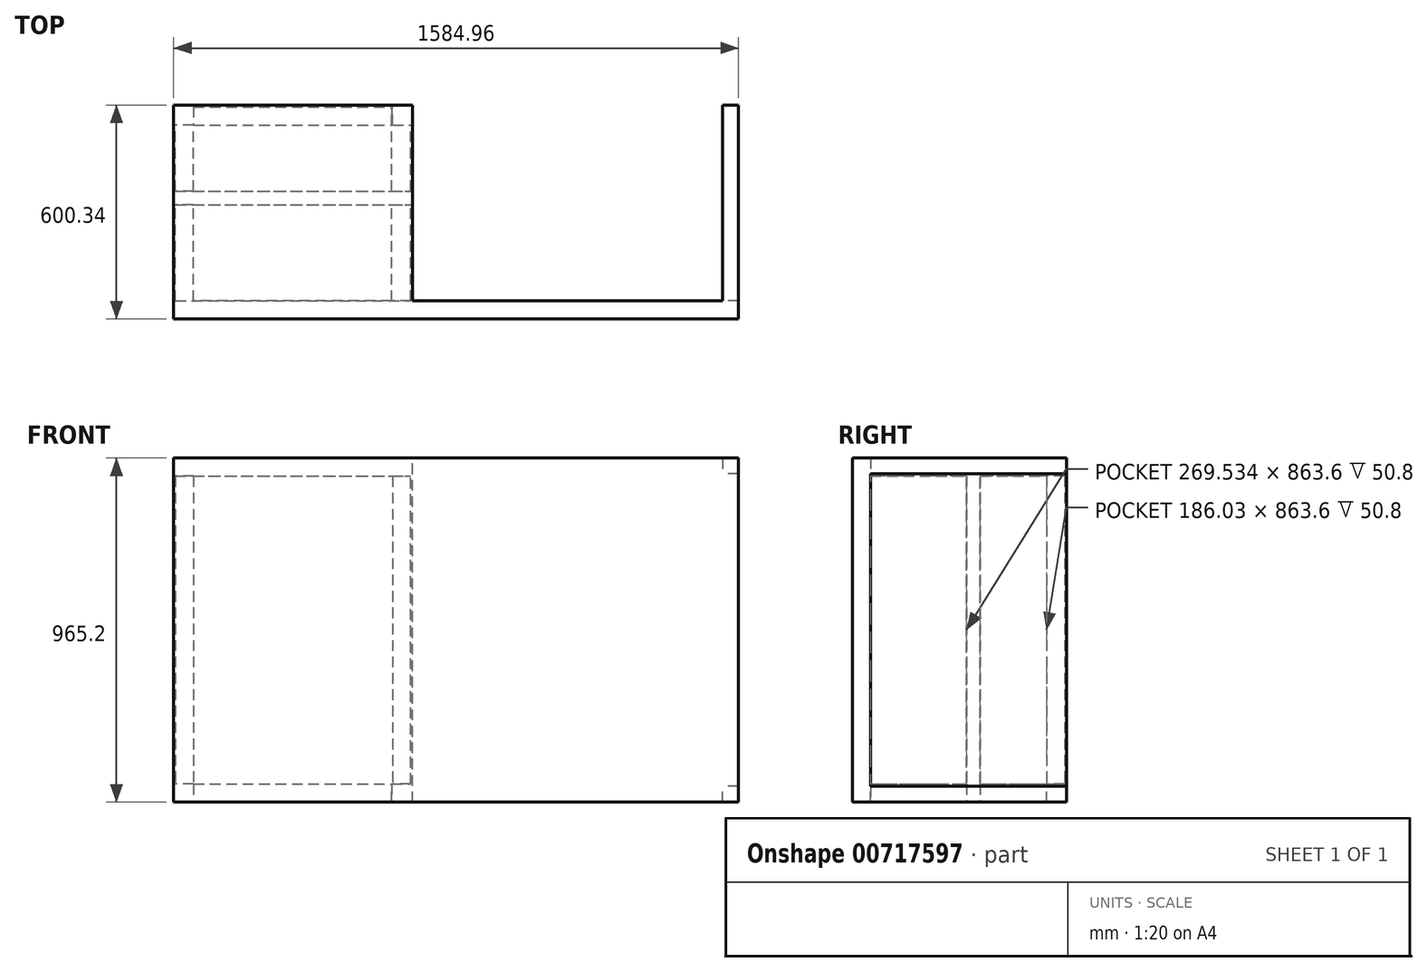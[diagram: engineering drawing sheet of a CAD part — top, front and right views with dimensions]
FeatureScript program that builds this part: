
annotation { "Feature Type Name" : "Feature", "Feature Type Description" : "" }
export const myFeature = defineFeature(function(context is Context, id is Id, definition is map)
    precondition{}
    {
        {
            var Q0;
            Q0=qCreatedBy(makeId("Top.planeOp"),FACE);
            var sketch = newSketch(context, id + "F0", { "sketchPlane" : qUnion([Q0])});
            skLineSegment(sketch, "E0.bottom", {"start": v(-609.6, -762) * mm, "end": v(609.6, -762) * mm});
            skLineSegment(sketch, "E0.top", {"start": v(-609.6, 762) * mm, "end": v(609.6, 762) * mm});
            skLineSegment(sketch, "E0.left", {"start": v(-609.6, -762) * mm, "end": v(-609.6, 762) * mm});
            skLineSegment(sketch, "E0.right", {"start": v(609.6, -762) * mm, "end": v(609.6, 762) * mm});
            skPoint(sketch, "E0.middle", {"position": v(0, 0) * mm});
            skLineSegment(sketch, "E1.0", {"start": v(660.4, -812.8) * mm, "end": v(660.4, 812.8) * mm});
            skLineSegment(sketch, "E1.1", {"start": v(-660.4, -812.8) * mm, "end": v(660.4, -812.8) * mm});
            skLineSegment(sketch, "E1.2", {"start": v(-660.4, -812.8) * mm, "end": v(-660.4, 812.8) * mm});
            skLineSegment(sketch, "E1.3", {"start": v(-660.4, 812.8) * mm, "end": v(660.4, 812.8) * mm});
            skSolve(sketch);
        }
        {
            var Q0;
            Q0=makeQuery(id+"F0.imprint","IMPRINT",FACE,{"disambiguationData":[TD([[makeQuery(id+"F0.imprint","IMPRINT",EDGE,{"derivedFrom":sQuery(id+"F0.wireOp",EDGE,"E0.bottom")}),-1.0]])]});
            extrude(context, id + "F1", {"entities" : qUnion([Q0]), "depth" : 50.8 * mm, "offsetDistance" : 25.4 * mm});
        }
        {
            var Q0;
            Q0=makeQuery(id+"F1.opExtrude","CAP_FACE",FACE,{"disambiguationData":[OSD([sQuery(id+"F0.wireOp",EDGE,"E0.bottom"),sQuery(id+"F0.wireOp",EDGE,"E0.top"),sQuery(id+"F0.wireOp",EDGE,"E0.left"),sQuery(id+"F0.wireOp",EDGE,"E0.right"),sQuery(id+"F0.wireOp",EDGE,"E1.0"),sQuery(id+"F0.wireOp",EDGE,"E1.1"),sQuery(id+"F0.wireOp",EDGE,"E1.2"),sQuery(id+"F0.wireOp",EDGE,"E1.3")])],"isStart":false});
            var sketch = newSketch(context, id + "F2", { "sketchPlane" : qUnion([Q0])});
            skLineSegment(sketch, "E2", {"start": v(-660.4, 812.8) * mm, "end": v(-609.6, 812.8) * mm});
            skLineSegment(sketch, "E3", {"start": v(-609.6, 812.8) * mm, "end": v(-609.6, 762) * mm});
            skLineSegment(sketch, "E4", {"start": v(-609.6, 762) * mm, "end": v(-660.4, 762) * mm});
            skLineSegment(sketch, "E5", {"start": v(-660.4, 762) * mm, "end": v(-660.4, 812.8) * mm});
            skLineSegment(sketch, "E6.MirrorCS", {"start": v(660.4, 812.8) * mm, "end": v(609.6, 812.8) * mm});
            skLineSegment(sketch, "E7.MirrorCS", {"start": v(609.6, 812.8) * mm, "end": v(609.6, 762) * mm});
            skLineSegment(sketch, "E8.MirrorCS", {"start": v(660.4, 762) * mm, "end": v(660.4, 812.8) * mm});
            skLineSegment(sketch, "E9.MirrorCS", {"start": v(609.6, 762) * mm, "end": v(660.4, 762) * mm});
            skLineSegment(sketch, "E10.MirrorCS", {"start": v(609.6, -762) * mm, "end": v(660.4, -762) * mm});
            skLineSegment(sketch, "E11.MirrorCS", {"start": v(-660.4, -812.8) * mm, "end": v(-609.6, -812.8) * mm});
            skLineSegment(sketch, "E12.MirrorCS", {"start": v(-609.6, -812.8) * mm, "end": v(-609.6, -762) * mm});
            skLineSegment(sketch, "E13.MirrorCS", {"start": v(660.4, -762) * mm, "end": v(660.4, -812.8) * mm});
            skLineSegment(sketch, "E14.MirrorCS", {"start": v(-609.6, -762) * mm, "end": v(-660.4, -762) * mm});
            skLineSegment(sketch, "E15.MirrorCS", {"start": v(609.6, -812.8) * mm, "end": v(609.6, -762) * mm});
            skLineSegment(sketch, "E16.MirrorCS", {"start": v(660.4, -812.8) * mm, "end": v(609.6, -812.8) * mm});
            skLineSegment(sketch, "E17.MirrorCS", {"start": v(-660.4, -762) * mm, "end": v(-660.4, -812.8) * mm});
            skSolve(sketch);
        }
        {
            var Q0;
            Q0=qSketchRegion(id+"F2",true);
            extrude(context, id + "F3", {"entities" : qUnion([Q0]), "operationType" : NewBodyOperationType.ADD, "depth" : 863.6 * mm, "offsetDistance" : 25.4 * mm});
        }
        {
            var Q0;
            Q0=makeQuery(id+"F3.opExtrude","CAP_FACE",FACE,{"disambiguationData":[OSD([sQuery(id+"F2.wireOp",EDGE,"E2"),sQuery(id+"F2.wireOp",EDGE,"E3"),sQuery(id+"F2.wireOp",EDGE,"E4"),sQuery(id+"F2.wireOp",EDGE,"E5")])],"isStart":false});
            var sketch = newSketch(context, id + "F4", { "sketchPlane" : qUnion([Q0])});
            skLineSegment(sketch, "E18.bottom", {"start": v(-609.6, -762) * mm, "end": v(609.6, -762) * mm});
            skLineSegment(sketch, "E18.top", {"start": v(-609.6, 762) * mm, "end": v(609.6, 762) * mm});
            skLineSegment(sketch, "E18.left", {"start": v(-609.6, -762) * mm, "end": v(-609.6, 762) * mm});
            skLineSegment(sketch, "E18.right", {"start": v(609.6, -762) * mm, "end": v(609.6, 762) * mm});
            skPoint(sketch, "E18.middle", {"position": v(0, 0) * mm});
            skLineSegment(sketch, "E19.0", {"start": v(-660.4, -812.8) * mm, "end": v(660.4, -812.8) * mm});
            skLineSegment(sketch, "E19.1", {"start": v(-660.4, -812.8) * mm, "end": v(-660.4, 812.8) * mm});
            skLineSegment(sketch, "E19.2", {"start": v(-660.4, 812.8) * mm, "end": v(660.4, 812.8) * mm});
            skLineSegment(sketch, "E19.3", {"start": v(660.4, -812.8) * mm, "end": v(660.4, 812.8) * mm});
            skSolve(sketch);
        }
        {
            var Q0;
            Q0=qSketchRegion(id+"F4",true);
            extrude(context, id + "F5", {"entities" : qUnion([Q0]), "operationType" : NewBodyOperationType.ADD, "depth" : 50.8 * mm, "offsetDistance" : 25.4 * mm});
        }
        {
            var Q0;
            Q0=makeQuery(id+"F5.opExtrude","SWEPT_FACE",FACE,{"disambiguationData":[OSD([sQuery(id+"F4.wireOp",EDGE,"E18.top")])]});
            var sketch = newSketch(context, id + "F6", { "sketchPlane" : qUnion([Q0])});
            skLineSegment(sketch, "E20", {"start": v(-609.6, 914.4) * mm, "end": v(-609.6, 965.2) * mm});
            skLineSegment(sketch, "E21", {"start": v(-609.6, 965.2) * mm, "end": v(0, 965.2) * mm});
            skLineSegment(sketch, "E22", {"start": v(0, 965.2) * mm, "end": v(0, 914.4) * mm});
            skLineSegment(sketch, "E23", {"start": v(0, 914.4) * mm, "end": v(-609.6, 914.4) * mm});
            skSolve(sketch);
        }
        {
            var Q0;
            Q0=qSketchRegion(id+"F6",true);
            extrude(context, id + "F7", {"entities" : qUnion([Q0]), "operationType" : NewBodyOperationType.ADD, "endBound" : BoundingType.UP_TO_NEXT, "depth" : 25.4 * mm, "offsetDistance" : 25.4 * mm});
        }
        {
            var Q0;
            Q0=makeQuery(id+"F7.boolean.opBoolean","MERGE",FACE,{"derivedFrom":[makeQuery(id+"F5.opExtrude","CAP_FACE",FACE,{"disambiguationData":[OSD([sQuery(id+"F4.wireOp",EDGE,"E18.bottom"),sQuery(id+"F4.wireOp",EDGE,"E18.top"),sQuery(id+"F4.wireOp",EDGE,"E18.left"),sQuery(id+"F4.wireOp",EDGE,"E18.right"),sQuery(id+"F4.wireOp",EDGE,"E19.0"),sQuery(id+"F4.wireOp",EDGE,"E19.1"),sQuery(id+"F4.wireOp",EDGE,"E19.2"),sQuery(id+"F4.wireOp",EDGE,"E19.3")])],"isStart":false}),makeQuery(id+"F7.opExtrude","SWEPT_FACE",FACE,{"disambiguationData":[OSD([sQuery(id+"F6.wireOp",EDGE,"E21")])]})]});
            var sketch = newSketch(context, id + "F8", { "sketchPlane" : qUnion([Q0])});
            skLineSegment(sketch, "E24", {"start": v(0, 762) * mm, "end": v(0, 812.8) * mm});
            skLineSegment(sketch, "E25", {"start": v(0, 812.8) * mm, "end": v(660.4, 812.8) * mm});
            skLineSegment(sketch, "E26", {"start": v(660.4, 812.8) * mm, "end": v(660.4, -812.8) * mm});
            skLineSegment(sketch, "E27", {"start": v(660.4, -812.8) * mm, "end": v(0, -812.8) * mm});
            skLineSegment(sketch, "E28", {"start": v(0, -812.8) * mm, "end": v(0, 762) * mm});
            skSolve(sketch);
        }
        {
            var Q0;
            Q0=qSketchRegion(id+"F8",true);
            extrude(context, id + "F9", {"entities" : qUnion([Q0]), "operationType" : NewBodyOperationType.REMOVE, "endBound" : BoundingType.THROUGH_ALL, "oppositeDirection" : true, "depth" : 25.4 * mm, "offsetDistance" : 25.4 * mm});
        }
        {
            var Q0;
            {var subQ0=sQuery(id+"F0.wireOp",EDGE,"E0.left");var subQ1=sQuery(id+"F0.wireOp",EDGE,"E1.3");var subQ2=sQuery(id+"F0.wireOp",EDGE,"E0.right");var subQ3=sQuery(id+"F0.wireOp",EDGE,"E0.top");var subQ4=makeQuery(id+"F1.opExtrude","CAP_FACE",FACE,{"disambiguationData":[OSD([sQuery(id+"F0.wireOp",EDGE,"E0.bottom"),subQ3,subQ0,subQ2,sQuery(id+"F0.wireOp",EDGE,"E1.0"),sQuery(id+"F0.wireOp",EDGE,"E1.1"),sQuery(id+"F0.wireOp",EDGE,"E1.2"),subQ1])],"isStart":false});Q0=makeQuery(id+"F3.boolean.opBoolean","SPLIT",FACE,{"disambiguationData":[TD([makeQuery(id+"F1.opExtrude","SWEPT_FACE",FACE,{"disambiguationData":[OSD([subQ1])]})])],"derivedFrom":subQ4});}
            var sketch = newSketch(context, id + "F10", { "sketchPlane" : qUnion([Q0])});
            skLineSegment(sketch, "E29", {"start": v(0, 812.8) * mm, "end": v(0, 762) * mm});
            skLineSegment(sketch, "E30", {"start": v(0, 762) * mm, "end": v(-50.8, 762) * mm});
            skLineSegment(sketch, "E31", {"start": v(-50.8, 762) * mm, "end": v(-50.8, 812.8) * mm});
            skLineSegment(sketch, "E32", {"start": v(-50.8, 812.8) * mm, "end": v(0, 812.8) * mm});
            skLineSegment(sketch, "E33.MirrorCS", {"start": v(-50.8, -812.8) * mm, "end": v(0, -812.8) * mm});
            skLineSegment(sketch, "E34.MirrorCS", {"start": v(0, -812.8) * mm, "end": v(0, -762) * mm});
            skLineSegment(sketch, "E35.MirrorCS", {"start": v(0, -762) * mm, "end": v(-50.8, -762) * mm});
            skLineSegment(sketch, "E36.MirrorCS", {"start": v(-50.8, -762) * mm, "end": v(-50.8, -812.8) * mm});
            skSolve(sketch);
        }
        {
            var Q0;
            Q0=qSketchRegion(id+"F10",true);
            extrude(context, id + "F11", {"entities" : qUnion([Q0]), "operationType" : NewBodyOperationType.ADD, "endBound" : BoundingType.UP_TO_NEXT, "depth" : 25.4 * mm, "offsetDistance" : 25.4 * mm});
        }
        {
            var Q0;
            {var subQ1=sQuery(id+"F0.wireOp",EDGE,"E0.top");var subQ7=sQuery(id+"F0.wireOp",EDGE,"E0.bottom");var subQ10=makeQuery(id+"F9.opExtrude","SWEPT_FACE",FACE,{"disambiguationData":[OSD([sQuery(id+"F8.wireOp",EDGE,"E24"),sQuery(id+"F8.wireOp",EDGE,"E28")])]});Q0=makeQuery(id+"FI0uP4kL5XJLF2I_1.boolean.opBoolean","MERGE",FACE,{"derivedFrom":[makeQuery(id+"F11.boolean.opBoolean","MERGE",FACE,{"derivedFrom":[makeQuery(id+"F9.boolean.opBoolean","MERGE",FACE,{"derivedFrom":[makeQuery(id+"F7.opExtrude","SWEPT_FACE",FACE,{"disambiguationData":[OSD([sQuery(id+"F6.wireOp",EDGE,"E22")])]}),subQ10]}),makeQuery(id+"F9.boolean.opBoolean","COPY",FACE,{"disambiguationData":[TD([makeQuery(id+"F1.opExtrude","SWEPT_FACE",FACE,{"disambiguationData":[OSD([subQ7])]})])],"derivedFrom":subQ10}),makeQuery(id+"F9.boolean.opBoolean","COPY",FACE,{"disambiguationData":[TD([makeQuery(id+"F1.opExtrude","SWEPT_FACE",FACE,{"disambiguationData":[OSD([subQ1])]})])],"derivedFrom":subQ10}),makeQuery(id+"F11.opExtrude","SWEPT_FACE",FACE,{"disambiguationData":[OSD([sQuery(id+"F10.wireOp",EDGE,"E29")])]}),makeQuery(id+"F11.opExtrude","SWEPT_FACE",FACE,{"disambiguationData":[OSD([sQuery(id+"F10.wireOp",EDGE,"E34.MirrorCS")])]})]}),makeQuery(id+"FI0uP4kL5XJLF2I_1.opExtrude","SWEPT_FACE",FACE,{"disambiguationData":[OSD([sQuery(id+"FPcTlZiTrbIZ70A_1.wireOp",EDGE,"L0GQmyvb-ReXV-Bmec-5JdH-0vrgJq4hWDGI")])]})]});}
            var sketch = newSketch(context, id + "F12", { "sketchPlane" : qUnion([Q0])});
            skLineSegment(sketch, "E37", {"start": v(812.8, 0) * mm, "end": v(254, 0) * mm});
            skLineSegment(sketch, "E38", {"start": v(254, 0) * mm, "end": v(254, 254) * mm});
            skLineSegment(sketch, "E39", {"start": v(254, 254) * mm, "end": v(812.8, 254) * mm});
            skLineSegment(sketch, "E40", {"start": v(812.8, 254) * mm, "end": v(812.8, 0) * mm});
            skSolve(sketch);
        }
        {
            var Q0;
            Q0=qSketchRegion(id+"F12",true);
            extrude(context, id + "F13", {"entities" : qUnion([Q0]), "operationType" : NewBodyOperationType.ADD, "depth" : 914.4 * mm, "offsetDistance" : 25.4 * mm});
        }
        {
            var Q0;
            Q0=makeQuery(id+"F13.boolean.opBoolean","MERGE",FACE,{"derivedFrom":[makeQuery(id+"F11.boolean.opBoolean","MERGE",FACE,{"derivedFrom":[makeQuery(id+"F5.boolean.opBoolean","MERGE",FACE,{"derivedFrom":[makeQuery(id+"F3.boolean.opBoolean","MERGE",FACE,{"derivedFrom":[makeQuery(id+"F1.opExtrude","SWEPT_FACE",FACE,{"disambiguationData":[OSD([sQuery(id+"F0.wireOp",EDGE,"E1.3")])]}),makeQuery(id+"F3.opExtrude","SWEPT_FACE",FACE,{"disambiguationData":[OSD([sQuery(id+"F2.wireOp",EDGE,"E2")])]}),makeQuery(id+"F3.opExtrude","SWEPT_FACE",FACE,{"disambiguationData":[OSD([sQuery(id+"F2.wireOp",EDGE,"E6.MirrorCS")])]})]}),makeQuery(id+"F5.opExtrude","SWEPT_FACE",FACE,{"disambiguationData":[OSD([sQuery(id+"F4.wireOp",EDGE,"E19.2")])]})]}),makeQuery(id+"F11.opExtrude","SWEPT_FACE",FACE,{"disambiguationData":[OSD([sQuery(id+"F10.wireOp",EDGE,"E32")])]})]}),makeQuery(id+"F13.opExtrude","SWEPT_FACE",FACE,{"disambiguationData":[OSD([sQuery(id+"F12.wireOp",EDGE,"E40")])]})]});
            var sketch = newSketch(context, id + "F14", { "sketchPlane" : qUnion([Q0])});
            skLineSegment(sketch, "E41.bottom", {"start": v(0, 254) * mm, "end": v(-914.4, 254) * mm});
            skLineSegment(sketch, "E41.top", {"start": v(0, 0) * mm, "end": v(-914.4, 0) * mm});
            skLineSegment(sketch, "E41.left", {"start": v(0, 254) * mm, "end": v(0, 0) * mm});
            skLineSegment(sketch, "E41.right", {"start": v(-914.4, 254) * mm, "end": v(-914.4, 0) * mm});
            skSolve(sketch);
        }
        {
            var Q0;
            Q0 = qSketchRegion(id + "F14", true);
            extrude(context, id + "F15", {"entities" : qUnion([Q0]), "operationType" : NewBodyOperationType.REMOVE, "endBound" : BoundingType.THROUGH_ALL, "oppositeDirection" : true, "depth" : 25.4 * mm, "offsetDistance" : 25.4 * mm});
        }
        {
            var Q0;
            {var subQ1=sQuery(id+"F0.wireOp",EDGE,"E0.top");var subQ7=sQuery(id+"F0.wireOp",EDGE,"E0.bottom");var subQ10=makeQuery(id+"F9.opExtrude","SWEPT_FACE",FACE,{"disambiguationData":[OSD([sQuery(id+"F8.wireOp",EDGE,"E24"),sQuery(id+"F8.wireOp",EDGE,"E28")])]});Q0=makeQuery(id+"F15.boolean.opBoolean","MERGE",FACE,{"derivedFrom":[makeQuery(id+"F11.boolean.opBoolean","MERGE",FACE,{"derivedFrom":[makeQuery(id+"F9.boolean.opBoolean","MERGE",FACE,{"derivedFrom":[makeQuery(id+"F7.opExtrude","SWEPT_FACE",FACE,{"disambiguationData":[OSD([sQuery(id+"F6.wireOp",EDGE,"E22")])]}),subQ10]}),makeQuery(id+"F9.boolean.opBoolean","COPY",FACE,{"disambiguationData":[TD([makeQuery(id+"F1.opExtrude","SWEPT_FACE",FACE,{"disambiguationData":[OSD([subQ7])]})])],"derivedFrom":subQ10}),makeQuery(id+"F9.boolean.opBoolean","COPY",FACE,{"disambiguationData":[TD([makeQuery(id+"F1.opExtrude","SWEPT_FACE",FACE,{"disambiguationData":[OSD([subQ1])]})])],"derivedFrom":subQ10}),makeQuery(id+"F11.opExtrude","SWEPT_FACE",FACE,{"disambiguationData":[OSD([sQuery(id+"F10.wireOp",EDGE,"E29")])]}),makeQuery(id+"F11.opExtrude","SWEPT_FACE",FACE,{"disambiguationData":[OSD([sQuery(id+"F10.wireOp",EDGE,"E34.MirrorCS")])]})]}),makeQuery(id+"F15.opExtrude","SWEPT_FACE",FACE,{"disambiguationData":[OSD([sQuery(id+"F14.wireOp",EDGE,"E41.left")])]})]});}
            var sketch = newSketch(context, id + "F16", { "sketchPlane" : qUnion([Q0])});
            skLineSegment(sketch, "E42.bottom", {"start": v(-812.8, 965.2) * mm, "end": v(812.8, 965.2) * mm});
            skLineSegment(sketch, "E42.top", {"start": v(-812.8, 0) * mm, "end": v(812.8, 0) * mm});
            skLineSegment(sketch, "E42.left", {"start": v(-812.8, 965.2) * mm, "end": v(-812.8, 0) * mm});
            skLineSegment(sketch, "E42.right", {"start": v(812.8, 965.2) * mm, "end": v(812.8, 0) * mm});
            skSolve(sketch);
        }
        {
            var Q0;
            Q0 = qSketchRegion(id + "F16", true);
            extrude(context, id + "F17", {"entities" : qUnion([Q0]), "operationType" : NewBodyOperationType.ADD, "surfaceOperationType" : NewSurfaceOperationType.ADD, "depth" : 5.08 * mm, "offsetDistance" : 25.4 * mm});
        }
        {
            var Q0;
            Q0=makeQuery(id+"F5.boolean.opBoolean","MERGE",FACE,{"derivedFrom":[makeQuery(id+"F3.boolean.opBoolean","MERGE",FACE,{"derivedFrom":[makeQuery(id+"F1.opExtrude","SWEPT_FACE",FACE,{"disambiguationData":[OSD([sQuery(id+"F0.wireOp",EDGE,"E1.2")])]}),makeQuery(id+"F3.opExtrude","SWEPT_FACE",FACE,{"disambiguationData":[OSD([sQuery(id+"F2.wireOp",EDGE,"E5")])]}),makeQuery(id+"F3.opExtrude","SWEPT_FACE",FACE,{"disambiguationData":[OSD([sQuery(id+"F2.wireOp",EDGE,"E17.MirrorCS")])]})]}),makeQuery(id+"F5.opExtrude","SWEPT_FACE",FACE,{"disambiguationData":[OSD([sQuery(id+"F4.wireOp",EDGE,"E19.1")])]})]});
            var sketch = newSketch(context, id + "F18", { "sketchPlane" : qUnion([Q0])});
            skLineSegment(sketch, "E43.bottom", {"start": v(-812.8, 965.2) * mm, "end": v(812.8, 965.2) * mm});
            skLineSegment(sketch, "E43.top", {"start": v(-812.8, 0) * mm, "end": v(812.8, 0) * mm});
            skLineSegment(sketch, "E43.left", {"start": v(-812.8, 965.2) * mm, "end": v(-812.8, 0) * mm});
            skLineSegment(sketch, "E43.right", {"start": v(812.8, 965.2) * mm, "end": v(812.8, 0) * mm});
            skSolve(sketch);
        }
        {
            var Q0;
            Q0 = qSketchRegion(id + "F18", true);
            extrude(context, id + "F19", {"entities" : qUnion([Q0]), "operationType" : NewBodyOperationType.ADD, "depth" : 5.08 * mm, "offsetDistance" : 25.4 * mm});
        }
        {
            var Q0;
            Q0=makeQuery(id+"F17.opExtrude","CAP_FACE",FACE,{"disambiguationData":[OSD([sQuery(id+"F16.wireOp",EDGE,"E42.bottom"),sQuery(id+"F16.wireOp",EDGE,"E42.top"),sQuery(id+"F16.wireOp",EDGE,"E42.left"),sQuery(id+"F16.wireOp",EDGE,"E42.right")])],"isStart":true});
            var sketch = newSketch(context, id + "F20", { "sketchPlane" : qUnion([Q0])});
            skLineSegment(sketch, "E44.bottom", {"start": v(811.74, 0) * mm, "end": v(-815.7, 0) * mm});
            skLineSegment(sketch, "E44.top", {"start": v(811.74, 51.7) * mm, "end": v(-815.7, 51.7) * mm});
            skLineSegment(sketch, "E44.left", {"start": v(811.74, 0) * mm, "end": v(811.74, 51.7) * mm});
            skLineSegment(sketch, "E44.right", {"start": v(-815.7, 0) * mm, "end": v(-815.7, 51.7) * mm});
            skSolve(sketch);
        }
        {
            var Q0;
            Q0 = qSketchRegion(id + "F20", true);
            extrude(context, id + "F21", {"entities" : qUnion([Q0]), "operationType" : NewBodyOperationType.ADD, "depth" : 53.34 * mm, "offsetDistance" : 25.4 * mm});
        }
        {
            var Q0;
            Q0=makeQuery(id+"F17.opExtrude","CAP_FACE",FACE,{"disambiguationData":[OSD([sQuery(id+"F16.wireOp",EDGE,"E42.bottom"),sQuery(id+"F16.wireOp",EDGE,"E42.top"),sQuery(id+"F16.wireOp",EDGE,"E42.left"),sQuery(id+"F16.wireOp",EDGE,"E42.right")])],"isStart":false});
            var sketch = newSketch(context, id + "F22", { "sketchPlane" : qUnion([Q0])});
            skLineSegment(sketch, "E45.bottom", {"start": v(217.54, 0) * mm, "end": v(268.34, 0) * mm});
            skLineSegment(sketch, "E45.top", {"start": v(217.54, 965.2) * mm, "end": v(268.34, 965.2) * mm});
            skLineSegment(sketch, "E45.left", {"start": v(217.54, 0) * mm, "end": v(217.54, 965.2) * mm});
            skLineSegment(sketch, "E45.right", {"start": v(268.34, 0) * mm, "end": v(268.34, 965.2) * mm});
            skSolve(sketch);
        }
        {
            var Q0;
            Q0 = qSketchRegion(id + "F22", true);
            var Q1;
            Q1=makeQuery(id+"F19.opExtrude","CAP_FACE",FACE,{"disambiguationData":[OSD([sQuery(id+"F18.wireOp",EDGE,"E43.bottom"),sQuery(id+"F18.wireOp",EDGE,"E43.top"),sQuery(id+"F18.wireOp",EDGE,"E43.left"),sQuery(id+"F18.wireOp",EDGE,"E43.right")])],"isStart":true});
            extrude(context, id + "F23", {"entities" : qUnion([Q0]), "operationType" : NewBodyOperationType.ADD, "depth" : 914.4 * mm, "offsetDistance" : 25.4 * mm, "hasSecondDirection" : true, "secondDirectionBound" : SecondDirectionBoundingType.UP_TO_SURFACE, "secondDirectionOppositeDirection" : true, "secondDirectionDepth" : 609.6 * mm, "secondDirectionBoundEntityFace" : qUnion([Q1])});
        }
        {
            var Q0;
            Q0=makeQuery(id+"F19.boolean.opBoolean","MERGE",FACE,{"derivedFrom":[makeQuery(id+"F17.boolean.opBoolean","MERGE",FACE,{"derivedFrom":[makeQuery(id+"F13.boolean.opBoolean","MERGE",FACE,{"derivedFrom":[makeQuery(id+"F11.boolean.opBoolean","MERGE",FACE,{"derivedFrom":[makeQuery(id+"F5.boolean.opBoolean","MERGE",FACE,{"derivedFrom":[makeQuery(id+"F3.boolean.opBoolean","MERGE",FACE,{"derivedFrom":[makeQuery(id+"F1.opExtrude","SWEPT_FACE",FACE,{"disambiguationData":[OSD([sQuery(id+"F0.wireOp",EDGE,"E1.3")])]}),makeQuery(id+"F3.opExtrude","SWEPT_FACE",FACE,{"disambiguationData":[OSD([sQuery(id+"F2.wireOp",EDGE,"E2")])]}),makeQuery(id+"F3.opExtrude","SWEPT_FACE",FACE,{"disambiguationData":[OSD([sQuery(id+"F2.wireOp",EDGE,"E6.MirrorCS")])]})]}),makeQuery(id+"F5.opExtrude","SWEPT_FACE",FACE,{"disambiguationData":[OSD([sQuery(id+"F4.wireOp",EDGE,"E19.2")])]})]}),makeQuery(id+"F11.opExtrude","SWEPT_FACE",FACE,{"disambiguationData":[OSD([sQuery(id+"F10.wireOp",EDGE,"E32")])]})]}),makeQuery(id+"F13.opExtrude","SWEPT_FACE",FACE,{"disambiguationData":[OSD([sQuery(id+"F12.wireOp",EDGE,"E40")])]})]}),makeQuery(id+"F17.opExtrude","SWEPT_FACE",FACE,{"disambiguationData":[OSD([sQuery(id+"F16.wireOp",EDGE,"E42.right")])]})]}),makeQuery(id+"F19.opExtrude","SWEPT_FACE",FACE,{"disambiguationData":[OSD([sQuery(id+"F18.wireOp",EDGE,"E43.left")])]})]});
            var sketch = newSketch(context, id + "F24", { "sketchPlane" : qUnion([Q0])});
            skLineSegment(sketch, "E46.bottom", {"start": v(665.48, 0) * mm, "end": v(-5.08, 0) * mm});
            skLineSegment(sketch, "E46.top", {"start": v(665.48, 965.2) * mm, "end": v(-5.08, 965.2) * mm});
            skLineSegment(sketch, "E46.left", {"start": v(665.48, 0) * mm, "end": v(665.48, 965.2) * mm});
            skLineSegment(sketch, "E46.right", {"start": v(-5.08, 0) * mm, "end": v(-5.08, 965.2) * mm});
            skSolve(sketch);
        }
        {
            var Q0;
            Q0 = qSketchRegion(id + "F24", true);
            extrude(context, id + "F25", {"entities" : qUnion([Q0]), "operationType" : NewBodyOperationType.ADD, "depth" : 5.08 * mm, "offsetDistance" : 25.4 * mm});
        }
        {
            var Q0;
            Q0=makeQuery(id+"F19.boolean.opBoolean","MERGE",FACE,{"derivedFrom":[makeQuery(id+"F17.boolean.opBoolean","MERGE",FACE,{"derivedFrom":[makeQuery(id+"F11.boolean.opBoolean","MERGE",FACE,{"derivedFrom":[makeQuery(id+"F5.boolean.opBoolean","MERGE",FACE,{"derivedFrom":[makeQuery(id+"F3.boolean.opBoolean","MERGE",FACE,{"derivedFrom":[makeQuery(id+"F1.opExtrude","SWEPT_FACE",FACE,{"disambiguationData":[OSD([sQuery(id+"F0.wireOp",EDGE,"E1.1")])]}),makeQuery(id+"F3.opExtrude","SWEPT_FACE",FACE,{"disambiguationData":[OSD([sQuery(id+"F2.wireOp",EDGE,"E11.MirrorCS")])]}),makeQuery(id+"F3.opExtrude","SWEPT_FACE",FACE,{"disambiguationData":[OSD([sQuery(id+"F2.wireOp",EDGE,"E16.MirrorCS")])]})]}),makeQuery(id+"F5.opExtrude","SWEPT_FACE",FACE,{"disambiguationData":[OSD([sQuery(id+"F4.wireOp",EDGE,"E19.0")])]})]}),makeQuery(id+"F11.opExtrude","SWEPT_FACE",FACE,{"disambiguationData":[OSD([sQuery(id+"F10.wireOp",EDGE,"E33.MirrorCS")])]})]}),makeQuery(id+"F17.opExtrude","SWEPT_FACE",FACE,{"disambiguationData":[OSD([sQuery(id+"F16.wireOp",EDGE,"E42.left")])]})]}),makeQuery(id+"F19.opExtrude","SWEPT_FACE",FACE,{"disambiguationData":[OSD([sQuery(id+"F18.wireOp",EDGE,"E43.right")])]})]});
            var sketch = newSketch(context, id + "F26", { "sketchPlane" : qUnion([Q0])});
            skLineSegment(sketch, "E47.bottom", {"start": v(-665.48, 965.2) * mm, "end": v(5.08, 965.2) * mm});
            skLineSegment(sketch, "E47.top", {"start": v(-665.48, 0) * mm, "end": v(5.08, 0) * mm});
            skLineSegment(sketch, "E47.left", {"start": v(-665.48, 965.2) * mm, "end": v(-665.48, 0) * mm});
            skLineSegment(sketch, "E47.right", {"start": v(5.08, 965.2) * mm, "end": v(5.08, 0) * mm});
            skSolve(sketch);
        }
        {
            var Q0;
            Q0 = qSketchRegion(id + "F26", true);
            extrude(context, id + "F27", {"entities" : qUnion([Q0]), "operationType" : NewBodyOperationType.ADD, "depth" : 5.08 * mm, "offsetDistance" : 25.4 * mm});
        }
        {
            var Q0;
            {var subQ2=sQuery(id+"F22.wireOp",EDGE,"E45.right");Q0=makeQuery(id+"F23.boolean.opBoolean","SPLIT",FACE,{"disambiguationData":[TD([makeQuery(id+"F7.opExtrude","SWEPT_FACE",FACE,{"disambiguationData":[OSD([sQuery(id+"F6.wireOp",EDGE,"E21")])]})])],"derivedFrom":makeQuery(id+"F23.opExtrude","SWEPT_FACE",FACE,{"disambiguationData":[OSD([subQ2])]})});}
            var sketch = newSketch(context, id + "F28", { "sketchPlane" : qUnion([Q0])});
            skLineSegment(sketch, "E48.bottom", {"start": v(-919.48, 0) * mm, "end": v(-875.03, 0) * mm});
            skLineSegment(sketch, "E48.top", {"start": v(-919.48, 44.45) * mm, "end": v(-875.03, 44.45) * mm});
            skLineSegment(sketch, "E48.left", {"start": v(-919.48, 0) * mm, "end": v(-919.48, 44.45) * mm});
            skLineSegment(sketch, "E48.right", {"start": v(-875.03, 0) * mm, "end": v(-875.03, 44.45) * mm});
            skLineSegment(sketch, "E49.bottom", {"start": v(-919.48, 965.2) * mm, "end": v(-875.03, 965.2) * mm});
            skLineSegment(sketch, "E49.top", {"start": v(-919.48, 920.75) * mm, "end": v(-875.03, 920.75) * mm});
            skLineSegment(sketch, "E49.left", {"start": v(-919.48, 965.2) * mm, "end": v(-919.48, 920.75) * mm});
            skLineSegment(sketch, "E49.right", {"start": v(-875.03, 965.2) * mm, "end": v(-875.03, 920.75) * mm});
            skSolve(sketch);
        }
        {
            var Q0;
            Q0 = qSketchRegion(id + "F28", true);
            var Q1;
            Q1=makeQuery(id+"F25.opExtrude","CAP_FACE",FACE,{"disambiguationData":[OSD([sQuery(id+"F24.wireOp",EDGE,"E46.bottom"),sQuery(id+"F24.wireOp",EDGE,"E46.top"),sQuery(id+"F24.wireOp",EDGE,"E46.left"),sQuery(id+"F24.wireOp",EDGE,"E46.right")])],"isStart":false});
            extrude(context, id + "F29", {"entities" : qUnion([Q0]), "operationType" : NewBodyOperationType.ADD, "endBound" : BoundingType.UP_TO_SURFACE, "depth" : 25.4 * mm, "endBoundEntityFace" : qUnion([Q1]), "offsetDistance" : 25.4 * mm});
        }
        {
            var Q0;
            Q0=makeQuery(id+"F29.boolean.opBoolean","MERGE",FACE,{"derivedFrom":[makeQuery(id+"F27.boolean.opBoolean","MERGE",FACE,{"derivedFrom":[makeQuery(id+"F25.boolean.opBoolean","MERGE",FACE,{"derivedFrom":[makeQuery(id+"F23.boolean.opBoolean","MERGE",FACE,{"derivedFrom":[makeQuery(id+"F21.boolean.opBoolean","MERGE",FACE,{"derivedFrom":[makeQuery(id+"F19.boolean.opBoolean","MERGE",FACE,{"derivedFrom":[makeQuery(id+"F17.boolean.opBoolean","MERGE",FACE,{"derivedFrom":[makeQuery(id+"F13.boolean.opBoolean","MERGE",FACE,{"derivedFrom":[makeQuery(id+"F1.opExtrude","CAP_FACE",FACE,{"disambiguationData":[OSD([sQuery(id+"F0.wireOp",EDGE,"E0.bottom"),sQuery(id+"F0.wireOp",EDGE,"E0.top"),sQuery(id+"F0.wireOp",EDGE,"E0.left"),sQuery(id+"F0.wireOp",EDGE,"E0.right"),sQuery(id+"F0.wireOp",EDGE,"E1.0"),sQuery(id+"F0.wireOp",EDGE,"E1.1"),sQuery(id+"F0.wireOp",EDGE,"E1.2"),sQuery(id+"F0.wireOp",EDGE,"E1.3")])],"isStart":true}),makeQuery(id+"F13.opExtrude","SWEPT_FACE",FACE,{"disambiguationData":[OSD([sQuery(id+"F12.wireOp",EDGE,"E37")])]})]}),makeQuery(id+"F17.opExtrude","SWEPT_FACE",FACE,{"disambiguationData":[OSD([sQuery(id+"F16.wireOp",EDGE,"E42.top")])]})]}),makeQuery(id+"F19.opExtrude","SWEPT_FACE",FACE,{"disambiguationData":[OSD([sQuery(id+"F18.wireOp",EDGE,"E43.top")])]})]}),makeQuery(id+"F21.opExtrude","SWEPT_FACE",FACE,{"disambiguationData":[OSD([sQuery(id+"F20.wireOp",EDGE,"E44.bottom")])]})]}),makeQuery(id+"F23.opExtrude","SWEPT_FACE",FACE,{"disambiguationData":[OSD([sQuery(id+"F22.wireOp",EDGE,"E45.bottom")])]})]}),makeQuery(id+"F25.opExtrude","SWEPT_FACE",FACE,{"disambiguationData":[OSD([sQuery(id+"F24.wireOp",EDGE,"E46.bottom")])]})]}),makeQuery(id+"F27.opExtrude","SWEPT_FACE",FACE,{"disambiguationData":[OSD([sQuery(id+"F26.wireOp",EDGE,"E47.top")])]})]}),makeQuery(id+"F29.opExtrude","SWEPT_FACE",FACE,{"disambiguationData":[OSD([sQuery(id+"F28.wireOp",EDGE,"E48.bottom")])]})]});
            var sketch = newSketch(context, id + "F30", { "sketchPlane" : qUnion([Q0])});
            skLineSegment(sketch, "E50.bottom", {"start": v(5.08, -217.54) * mm, "end": v(-665.48, -217.54) * mm});
            skLineSegment(sketch, "E50.top", {"start": v(5.08, 817.88) * mm, "end": v(-665.48, 817.88) * mm});
            skLineSegment(sketch, "E50.left", {"start": v(5.08, -217.54) * mm, "end": v(5.08, 817.88) * mm});
            skLineSegment(sketch, "E50.right", {"start": v(-665.48, -217.54) * mm, "end": v(-665.48, 817.88) * mm});
            skSolve(sketch);
        }
        {
            var Q0;
            Q0 = qSketchRegion(id + "F30", true);
            extrude(context, id + "F31", {"entities" : qUnion([Q0]), "operationType" : NewBodyOperationType.REMOVE, "endBound" : BoundingType.THROUGH_ALL, "oppositeDirection" : true, "depth" : 25.4 * mm, "offsetDistance" : 25.4 * mm});
        }
        {
            var Q0;
            Q0=makeQuery(id+"F29.boolean.opBoolean","MERGE",FACE,{"derivedFrom":[makeQuery(id+"F27.boolean.opBoolean","MERGE",FACE,{"derivedFrom":[makeQuery(id+"F25.boolean.opBoolean","MERGE",FACE,{"derivedFrom":[makeQuery(id+"F23.boolean.opBoolean","MERGE",FACE,{"derivedFrom":[makeQuery(id+"F21.boolean.opBoolean","MERGE",FACE,{"derivedFrom":[makeQuery(id+"F19.boolean.opBoolean","MERGE",FACE,{"derivedFrom":[makeQuery(id+"F17.boolean.opBoolean","MERGE",FACE,{"derivedFrom":[makeQuery(id+"F13.boolean.opBoolean","MERGE",FACE,{"derivedFrom":[makeQuery(id+"F1.opExtrude","CAP_FACE",FACE,{"disambiguationData":[OSD([sQuery(id+"F0.wireOp",EDGE,"E0.bottom"),sQuery(id+"F0.wireOp",EDGE,"E0.top"),sQuery(id+"F0.wireOp",EDGE,"E0.left"),sQuery(id+"F0.wireOp",EDGE,"E0.right"),sQuery(id+"F0.wireOp",EDGE,"E1.0"),sQuery(id+"F0.wireOp",EDGE,"E1.1"),sQuery(id+"F0.wireOp",EDGE,"E1.2"),sQuery(id+"F0.wireOp",EDGE,"E1.3")])],"isStart":true}),makeQuery(id+"F13.opExtrude","SWEPT_FACE",FACE,{"disambiguationData":[OSD([sQuery(id+"F12.wireOp",EDGE,"E37")])]})]}),makeQuery(id+"F17.opExtrude","SWEPT_FACE",FACE,{"disambiguationData":[OSD([sQuery(id+"F16.wireOp",EDGE,"E42.top")])]})]}),makeQuery(id+"F19.opExtrude","SWEPT_FACE",FACE,{"disambiguationData":[OSD([sQuery(id+"F18.wireOp",EDGE,"E43.top")])]})]}),makeQuery(id+"F21.opExtrude","SWEPT_FACE",FACE,{"disambiguationData":[OSD([sQuery(id+"F20.wireOp",EDGE,"E44.bottom")])]})]}),makeQuery(id+"F23.opExtrude","SWEPT_FACE",FACE,{"disambiguationData":[OSD([sQuery(id+"F22.wireOp",EDGE,"E45.bottom")])]})]}),makeQuery(id+"F25.opExtrude","SWEPT_FACE",FACE,{"disambiguationData":[OSD([sQuery(id+"F24.wireOp",EDGE,"E46.bottom")])]})]}),makeQuery(id+"F27.opExtrude","SWEPT_FACE",FACE,{"disambiguationData":[OSD([sQuery(id+"F26.wireOp",EDGE,"E47.top")])]})]}),makeQuery(id+"F29.opExtrude","SWEPT_FACE",FACE,{"disambiguationData":[OSD([sQuery(id+"F28.wireOp",EDGE,"E48.bottom")])]})]});
            var sketch = newSketch(context, id + "F32", { "sketchPlane" : qUnion([Q0])});
            skLineSegment(sketch, "E51.bottom", {"start": v(-665.48, -537.87) * mm, "end": v(5.08, -537.87) * mm});
            skLineSegment(sketch, "E51.top", {"start": v(-665.48, -575.97) * mm, "end": v(5.08, -575.97) * mm});
            skLineSegment(sketch, "E51.left", {"start": v(-665.48, -537.87) * mm, "end": v(-665.48, -575.97) * mm});
            skLineSegment(sketch, "E51.right", {"start": v(5.08, -537.87) * mm, "end": v(5.08, -575.97) * mm});
            skSolve(sketch);
        }
        {
            var Q0;
            Q0 = qSketchRegion(id + "F32", true);
            var Q1;
            {var subQ2=sQuery(id+"F4.wireOp",EDGE,"E19.2");var subQ5=makeQuery(id+"F1.opExtrude","SWEPT_FACE",FACE,{"disambiguationData":[OSD([sQuery(id+"F0.wireOp",EDGE,"E1.3")])]});var subQ9=sQuery(id+"F4.wireOp",EDGE,"E18.top");var subQ11=sQuery(id+"F4.wireOp",EDGE,"E19.1");var subQ12=sQuery(id+"F4.wireOp",EDGE,"E19.0");var subQ13=sQuery(id+"F4.wireOp",EDGE,"E18.right");var subQ14=sQuery(id+"F4.wireOp",EDGE,"E18.left");var subQ15=sQuery(id+"F4.wireOp",EDGE,"E18.bottom");var subQ16=makeQuery(id+"F5.opExtrude","CAP_FACE",FACE,{"disambiguationData":[OSD([subQ15,subQ9,subQ14,subQ13,subQ12,subQ11,subQ2,sQuery(id+"F4.wireOp",EDGE,"E19.3")])],"isStart":true});Q1=makeQuery(id+"F23.boolean.opBoolean","SPLIT",FACE,{"disambiguationData":[TD([makeQuery(id+"F1.opExtrude","SWEPT_FACE",FACE,{"disambiguationData":[OSD([sQuery(id+"F0.wireOp",EDGE,"E0.top")])]})])],"derivedFrom":makeQuery(id+"F7.boolean.opBoolean","MERGE",FACE,{"derivedFrom":[makeQuery(id+"F5.boolean.opBoolean","SPLIT",FACE,{"disambiguationData":[TD([makeQuery(id+"F1.opExtrude","SWEPT_FACE",FACE,{"disambiguationData":[OSD([sQuery(id+"F0.wireOp",EDGE,"E1.1")])]})])],"derivedFrom":subQ16}),makeQuery(id+"F5.boolean.opBoolean","SPLIT",FACE,{"disambiguationData":[TD([subQ5])],"derivedFrom":subQ16}),makeQuery(id+"F5.boolean.opBoolean","SPLIT",FACE,{"disambiguationData":[TD([makeQuery(id+"F1.opExtrude","SWEPT_FACE",FACE,{"disambiguationData":[OSD([sQuery(id+"F0.wireOp",EDGE,"E1.2")])]})])],"derivedFrom":subQ16}),makeQuery(id+"F7.opExtrude","SWEPT_FACE",FACE,{"disambiguationData":[OSD([sQuery(id+"F6.wireOp",EDGE,"E23")])]})]})});}
            extrude(context, id + "F33", {"entities" : qUnion([Q0]), "operationType" : NewBodyOperationType.ADD, "endBound" : BoundingType.UP_TO_SURFACE, "oppositeDirection" : true, "depth" : 25.4 * mm, "endBoundEntityFace" : qUnion([Q1]), "offsetDistance" : 25.4 * mm});
        }
    });
